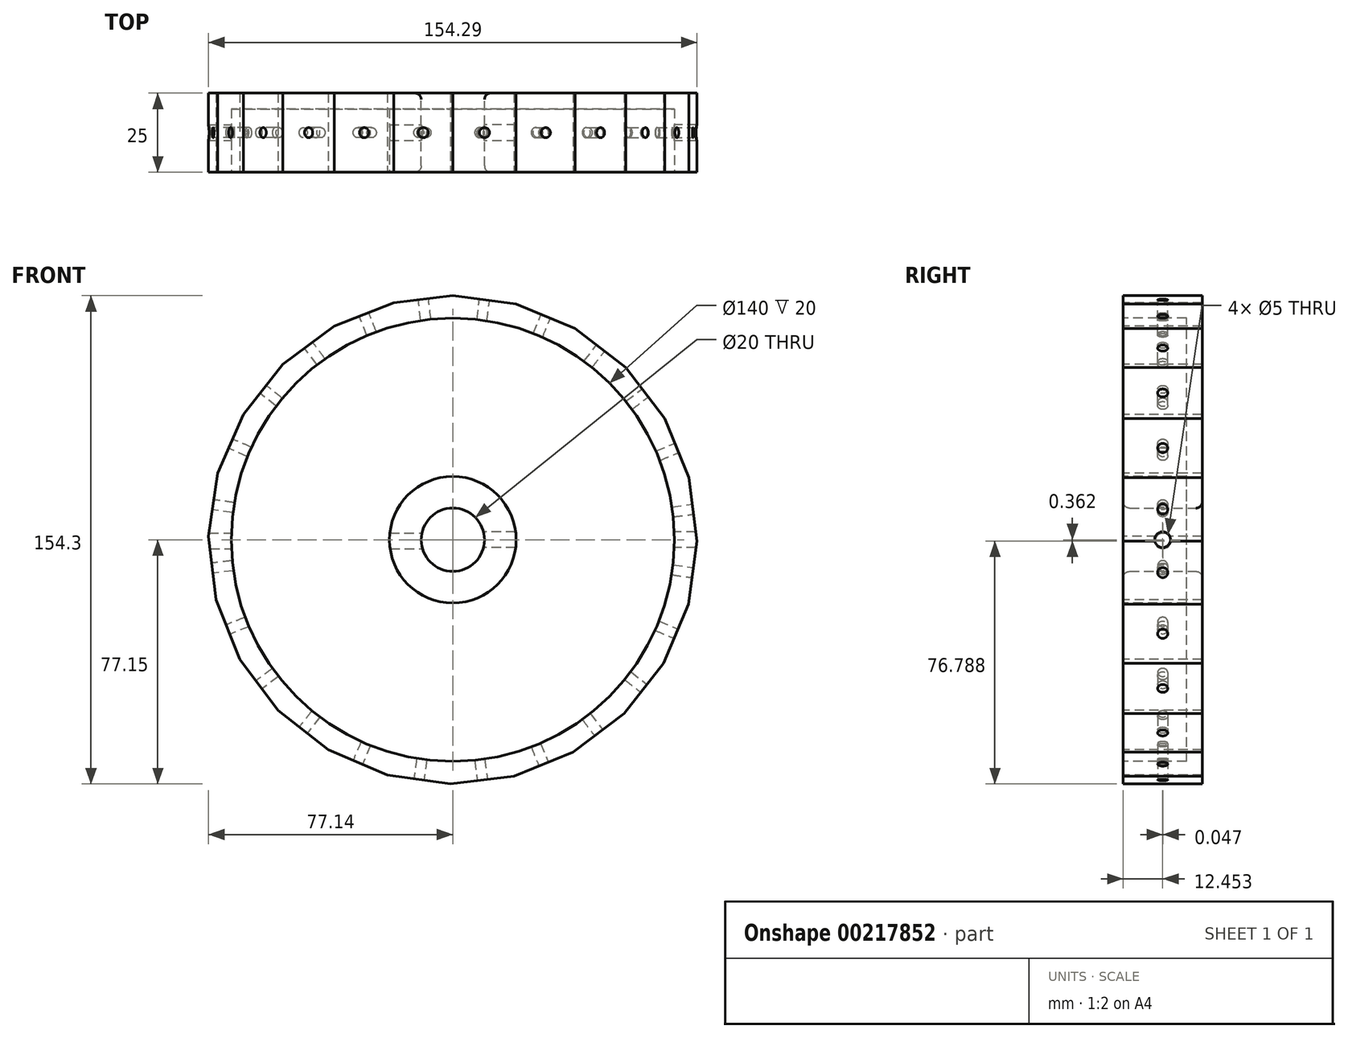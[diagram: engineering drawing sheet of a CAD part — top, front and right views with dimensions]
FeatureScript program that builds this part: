
annotation { "Feature Type Name" : "Feature", "Feature Type Description" : "" }
export const myFeature = defineFeature(function(context is Context, id is Id, definition is map)
    precondition{}
    {
        {
            var Q0;
            Q0=qCreatedBy(makeId("Front.planeOp"),FACE);
            var sketch = newSketch(context, id + "F0", { "sketchPlane" : qUnion([Q0])});
            skCircle(sketch, "E0", {"center": v(0, 0) * mm, "radius": 77.15 * mm});
            skCircle(sketch, "E1", {"center": v(0, 0) * mm, "radius": 10 * mm});
            skSolve(sketch);
        }
        {
            var Q0;
            Q0 = qSketchRegion(id + "F0", true);
            extrude(context, id + "F1", {"entities" : qUnion([Q0]), "depth" : 25 * mm});
        }
        {
            var Q0;
            Q0=makeQuery(id+"F1.opExtrude","CAP_FACE",FACE,{"disambiguationData":[OSD([sQuery(id+"F0.wireOp",EDGE,"E0"),sQuery(id+"F0.wireOp",EDGE,"E1")])],"isStart":false});
            var sketch = newSketch(context, id + "F2", { "sketchPlane" : qUnion([Q0])});
            skLineSegment(sketch, "E2", {"start": v(0, 0) * mm, "end": v(0, 77.15) * mm});
            skLineSegment(sketch, "E3", {"start": v(0, 0) * mm, "end": v(20.03, 74.5) * mm});
            skLineSegment(sketch, "E4", {"start": v(0, 77.15) * mm, "end": v(20.03, 74.5) * mm});
            skLineSegment(sketch, "E5", {"start": v(0, 0) * mm, "end": v(38.68, 66.75) * mm});
            skLineSegment(sketch, "E6", {"start": v(20.03, 74.5) * mm, "end": v(38.68, 66.75) * mm});
            skLineSegment(sketch, "E7", {"start": v(0, 0) * mm, "end": v(54.68, 54.43) * mm});
            skLineSegment(sketch, "E8", {"start": v(38.68, 66.75) * mm, "end": v(54.68, 54.43) * mm});
            skLineSegment(sketch, "E9", {"start": v(0, 0) * mm, "end": v(66.93, 38.37) * mm});
            skLineSegment(sketch, "E10", {"start": v(54.68, 54.43) * mm, "end": v(66.93, 38.37) * mm});
            skLineSegment(sketch, "E11", {"start": v(0, 0) * mm, "end": v(74.6, 19.68) * mm});
            skLineSegment(sketch, "E12", {"start": v(74.6, 19.68) * mm, "end": v(66.93, 38.37) * mm});
            skLineSegment(sketch, "E13", {"start": v(0, 0) * mm, "end": v(77.15, -0.36) * mm});
            skLineSegment(sketch, "E14", {"start": v(77.15, -0.36) * mm, "end": v(74.6, 19.68) * mm});
            skLineSegment(sketch, "E15", {"start": v(0, 0) * mm, "end": v(74.41, -20.38) * mm});
            skLineSegment(sketch, "E16", {"start": v(74.41, -20.38) * mm, "end": v(77.15, -0.36) * mm});
            skLineSegment(sketch, "E17", {"start": v(0, 0) * mm, "end": v(66.57, -39) * mm});
            skLineSegment(sketch, "E18", {"start": v(66.57, -39) * mm, "end": v(74.41, -20.38) * mm});
            skLineSegment(sketch, "E19", {"start": v(0, 0) * mm, "end": v(54.17, -54.94) * mm});
            skLineSegment(sketch, "E20", {"start": v(54.17, -54.94) * mm, "end": v(66.57, -39) * mm});
            skLineSegment(sketch, "E21", {"start": v(0, 0) * mm, "end": v(38.05, -67.11) * mm});
            skLineSegment(sketch, "E22", {"start": v(38.05, -67.11) * mm, "end": v(54.17, -54.94) * mm});
            skLineSegment(sketch, "E23", {"start": v(0, 0) * mm, "end": v(19.33, -74.7) * mm});
            skLineSegment(sketch, "E24", {"start": v(19.33, -74.7) * mm, "end": v(38.05, -67.11) * mm});
            skLineSegment(sketch, "E25", {"start": v(0, 0) * mm, "end": v(-0.72, -77.15) * mm});
            skLineSegment(sketch, "E26", {"start": v(-0.72, -77.15) * mm, "end": v(19.33, -74.7) * mm});
            skLineSegment(sketch, "E27", {"start": v(0, 0) * mm, "end": v(-20.72, -74.31) * mm});
            skLineSegment(sketch, "E28", {"start": v(-20.72, -74.31) * mm, "end": v(-0.72, -77.15) * mm});
            skLineSegment(sketch, "E29", {"start": v(0, 0) * mm, "end": v(-39.3, -66.39) * mm});
            skLineSegment(sketch, "E30", {"start": v(-39.3, -66.39) * mm, "end": v(-20.72, -74.31) * mm});
            skLineSegment(sketch, "E31", {"start": v(0, 0) * mm, "end": v(-55.19, -53.9) * mm});
            skLineSegment(sketch, "E32", {"start": v(-55.19, -53.9) * mm, "end": v(-39.3, -66.39) * mm});
            skLineSegment(sketch, "E33", {"start": v(0, 0) * mm, "end": v(-67.3, -37.74) * mm});
            skLineSegment(sketch, "E34", {"start": v(-67.3, -37.74) * mm, "end": v(-55.19, -53.9) * mm});
            skLineSegment(sketch, "E35", {"start": v(0, 0) * mm, "end": v(-74.78, -18.98) * mm});
            skLineSegment(sketch, "E36", {"start": v(-74.78, -18.98) * mm, "end": v(-67.3, -37.74) * mm});
            skLineSegment(sketch, "E37", {"start": v(0, 0) * mm, "end": v(-77.14, 1.09) * mm});
            skLineSegment(sketch, "E38", {"start": v(-77.14, 1.09) * mm, "end": v(-74.78, -18.98) * mm});
            skLineSegment(sketch, "E39", {"start": v(0, 0) * mm, "end": v(-74.22, 21.07) * mm});
            skLineSegment(sketch, "E40", {"start": v(-74.22, 21.07) * mm, "end": v(-77.14, 1.09) * mm});
            skLineSegment(sketch, "E41", {"start": v(0, 0) * mm, "end": v(-66.2, 39.62) * mm});
            skLineSegment(sketch, "E42", {"start": v(-66.2, 39.62) * mm, "end": v(-74.22, 21.07) * mm});
            skLineSegment(sketch, "E43", {"start": v(0, 0) * mm, "end": v(-53.65, 55.44) * mm});
            skLineSegment(sketch, "E44", {"start": v(-53.65, 55.44) * mm, "end": v(-66.2, 39.62) * mm});
            skLineSegment(sketch, "E45", {"start": v(0, 0) * mm, "end": v(-37.42, 67.47) * mm});
            skLineSegment(sketch, "E46", {"start": v(-37.42, 67.47) * mm, "end": v(-53.65, 55.44) * mm});
            skLineSegment(sketch, "E47", {"start": v(0, 0) * mm, "end": v(-18.62, 74.87) * mm});
            skLineSegment(sketch, "E48", {"start": v(-18.62, 74.87) * mm, "end": v(-37.42, 67.47) * mm});
            skLineSegment(sketch, "E49", {"start": v(-18.62, 74.87) * mm, "end": v(0, 77.15) * mm});
            skSolve(sketch);
        }
        {
            var Q0;
            {var subQ0=sQuery(id+"F2.wireOp",EDGE,"E4");Q0=makeQuery(id+"F2.imprint","IMPRINT",FACE,{"disambiguationData":[TD([[makeQuery(id+"F2.imprint","IMPRINT",EDGE,{"derivedFrom":subQ0}),1.0]])]});}
            var Q1;
            {var subQ0=sQuery(id+"F2.wireOp",EDGE,"E6");Q1=makeQuery(id+"F2.imprint","IMPRINT",FACE,{"disambiguationData":[TD([[makeQuery(id+"F2.imprint","IMPRINT",EDGE,{"derivedFrom":subQ0}),1.0]])]});}
            var Q2;
            {var subQ0=sQuery(id+"F2.wireOp",EDGE,"E8");Q2=makeQuery(id+"F2.imprint","IMPRINT",FACE,{"disambiguationData":[TD([[makeQuery(id+"F2.imprint","IMPRINT",EDGE,{"derivedFrom":subQ0}),1.0]])]});}
            var Q3;
            {var subQ0=sQuery(id+"F2.wireOp",EDGE,"E10");Q3=makeQuery(id+"F2.imprint","IMPRINT",FACE,{"disambiguationData":[TD([[makeQuery(id+"F2.imprint","IMPRINT",EDGE,{"derivedFrom":subQ0}),1.0]])]});}
            var Q4;
            {var subQ0=sQuery(id+"F2.wireOp",EDGE,"E12");Q4=makeQuery(id+"F2.imprint","IMPRINT",FACE,{"disambiguationData":[TD([[makeQuery(id+"F2.imprint","IMPRINT",EDGE,{"derivedFrom":subQ0}),-1.0]])]});}
            var Q5;
            {var subQ0=sQuery(id+"F2.wireOp",EDGE,"E14");Q5=makeQuery(id+"F2.imprint","IMPRINT",FACE,{"disambiguationData":[TD([[makeQuery(id+"F2.imprint","IMPRINT",EDGE,{"derivedFrom":subQ0}),-1.0]])]});}
            var Q6;
            {var subQ0=sQuery(id+"F2.wireOp",EDGE,"E16");Q6=makeQuery(id+"F2.imprint","IMPRINT",FACE,{"disambiguationData":[TD([[makeQuery(id+"F2.imprint","IMPRINT",EDGE,{"derivedFrom":subQ0}),-1.0]])]});}
            var Q7;
            {var subQ0=sQuery(id+"F2.wireOp",EDGE,"E18");Q7=makeQuery(id+"F2.imprint","IMPRINT",FACE,{"disambiguationData":[TD([[makeQuery(id+"F2.imprint","IMPRINT",EDGE,{"derivedFrom":subQ0}),-1.0]])]});}
            var Q8;
            {var subQ0=sQuery(id+"F2.wireOp",EDGE,"E20");Q8=makeQuery(id+"F2.imprint","IMPRINT",FACE,{"disambiguationData":[TD([[makeQuery(id+"F2.imprint","IMPRINT",EDGE,{"derivedFrom":subQ0}),-1.0]])]});}
            var Q9;
            {var subQ0=sQuery(id+"F2.wireOp",EDGE,"E22");Q9=makeQuery(id+"F2.imprint","IMPRINT",FACE,{"disambiguationData":[TD([[makeQuery(id+"F2.imprint","IMPRINT",EDGE,{"derivedFrom":subQ0}),-1.0]])]});}
            var Q10;
            {var subQ0=sQuery(id+"F2.wireOp",EDGE,"E24");Q10=makeQuery(id+"F2.imprint","IMPRINT",FACE,{"disambiguationData":[TD([[makeQuery(id+"F2.imprint","IMPRINT",EDGE,{"derivedFrom":subQ0}),-1.0]])]});}
            var Q11;
            {var subQ0=sQuery(id+"F2.wireOp",EDGE,"E26");Q11=makeQuery(id+"F2.imprint","IMPRINT",FACE,{"disambiguationData":[TD([[makeQuery(id+"F2.imprint","IMPRINT",EDGE,{"derivedFrom":subQ0}),-1.0]])]});}
            var Q12;
            {var subQ0=sQuery(id+"F2.wireOp",EDGE,"E28");Q12=makeQuery(id+"F2.imprint","IMPRINT",FACE,{"disambiguationData":[TD([[makeQuery(id+"F2.imprint","IMPRINT",EDGE,{"derivedFrom":subQ0}),-1.0]])]});}
            var Q13;
            {var subQ0=sQuery(id+"F2.wireOp",EDGE,"E30");Q13=makeQuery(id+"F2.imprint","IMPRINT",FACE,{"disambiguationData":[TD([[makeQuery(id+"F2.imprint","IMPRINT",EDGE,{"derivedFrom":subQ0}),-1.0]])]});}
            var Q14;
            {var subQ0=sQuery(id+"F2.wireOp",EDGE,"E32");Q14=makeQuery(id+"F2.imprint","IMPRINT",FACE,{"disambiguationData":[TD([[makeQuery(id+"F2.imprint","IMPRINT",EDGE,{"derivedFrom":subQ0}),-1.0]])]});}
            var Q15;
            {var subQ0=sQuery(id+"F2.wireOp",EDGE,"E34");Q15=makeQuery(id+"F2.imprint","IMPRINT",FACE,{"disambiguationData":[TD([[makeQuery(id+"F2.imprint","IMPRINT",EDGE,{"derivedFrom":subQ0}),-1.0]])]});}
            var Q16;
            {var subQ0=sQuery(id+"F2.wireOp",EDGE,"E36");Q16=makeQuery(id+"F2.imprint","IMPRINT",FACE,{"disambiguationData":[TD([[makeQuery(id+"F2.imprint","IMPRINT",EDGE,{"derivedFrom":subQ0}),-1.0]])]});}
            var Q17;
            {var subQ0=sQuery(id+"F2.wireOp",EDGE,"E38");Q17=makeQuery(id+"F2.imprint","IMPRINT",FACE,{"disambiguationData":[TD([[makeQuery(id+"F2.imprint","IMPRINT",EDGE,{"derivedFrom":subQ0}),-1.0]])]});}
            var Q18;
            {var subQ0=sQuery(id+"F2.wireOp",EDGE,"E40");Q18=makeQuery(id+"F2.imprint","IMPRINT",FACE,{"disambiguationData":[TD([[makeQuery(id+"F2.imprint","IMPRINT",EDGE,{"derivedFrom":subQ0}),-1.0]])]});}
            var Q19;
            {var subQ0=sQuery(id+"F2.wireOp",EDGE,"E42");Q19=makeQuery(id+"F2.imprint","IMPRINT",FACE,{"disambiguationData":[TD([[makeQuery(id+"F2.imprint","IMPRINT",EDGE,{"derivedFrom":subQ0}),-1.0]])]});}
            var Q20;
            {var subQ0=sQuery(id+"F2.wireOp",EDGE,"E44");Q20=makeQuery(id+"F2.imprint","IMPRINT",FACE,{"disambiguationData":[TD([[makeQuery(id+"F2.imprint","IMPRINT",EDGE,{"derivedFrom":subQ0}),-1.0]])]});}
            var Q21;
            {var subQ0=sQuery(id+"F2.wireOp",EDGE,"E46");Q21=makeQuery(id+"F2.imprint","IMPRINT",FACE,{"disambiguationData":[TD([[makeQuery(id+"F2.imprint","IMPRINT",EDGE,{"derivedFrom":subQ0}),-1.0]])]});}
            var Q22;
            {var subQ0=sQuery(id+"F2.wireOp",EDGE,"E48");Q22=makeQuery(id+"F2.imprint","IMPRINT",FACE,{"disambiguationData":[TD([[makeQuery(id+"F2.imprint","IMPRINT",EDGE,{"derivedFrom":subQ0}),-1.0]])]});}
            var Q23;
            {var subQ0=sQuery(id+"F2.wireOp",EDGE,"E49");Q23=makeQuery(id+"F2.imprint","IMPRINT",FACE,{"disambiguationData":[TD([[makeQuery(id+"F2.imprint","IMPRINT",EDGE,{"derivedFrom":subQ0}),1.0]])]});}
            extrude(context, id + "F3", {"entities" : qUnion([Q0, Q1, Q2, Q3, Q4, Q5, Q6, Q7, Q8, Q9, Q10, Q11, Q12, Q13, Q14, Q15, Q16, Q17, Q18, Q19, Q20, Q21, Q22, Q23]), "operationType" : NewBodyOperationType.REMOVE, "oppositeDirection" : true, "depth" : 25 * mm});
        }
        {
            var Q0;
            Q0=makeQuery(id+"F1.opExtrude","CAP_FACE",FACE,{"disambiguationData":[OSD([sQuery(id+"F0.wireOp",EDGE,"E0"),sQuery(id+"F0.wireOp",EDGE,"E1")])],"isStart":false});
            var sketch = newSketch(context, id + "F4", { "sketchPlane" : qUnion([Q0])});
            skCircle(sketch, "E50", {"center": v(0, 0) * mm, "radius": 10 * mm});
            skCircle(sketch, "E51", {"center": v(0, 0) * mm, "radius": 20 * mm});
            skCircle(sketch, "E52", {"center": v(0, 0) * mm, "radius": 70 * mm});
            skSolve(sketch);
        }
        {
            var Q0;
            Q0=makeQuery(id+"F4.imprint","IMPRINT",FACE,{"disambiguationData":[TD([[makeQuery(id+"F4.imprint","IMPRINT",EDGE,{"derivedFrom":sQuery(id+"F4.wireOp",EDGE,"E51")}),-1.0]])]});
            extrude(context, id + "F5", {"entities" : qUnion([Q0]), "operationType" : NewBodyOperationType.REMOVE, "oppositeDirection" : true, "depth" : 20 * mm});
        }
        {
            var Q0;
            Q0=makeQuery(id+"F1.opExtrude","CAP_EDGE",EDGE,{"disambiguationData":[OSD([sQuery(id+"F0.wireOp",EDGE,"E1")])],"isStart":true});
            var Q1;
            Q1=makeQuery(id+"F1.opExtrude","CAP_EDGE",EDGE,{"disambiguationData":[OSD([sQuery(id+"F0.wireOp",EDGE,"E1")])],"isStart":false});
            fillet(context, id + "F6", {"entities" : qUnion([Q0, Q1]), "radius" : 2 * mm, "tangentPropagation" : true, "allowEdgeOverflow" : false});
        }
        {
            var Q0;
            Q0=makeQuery(id+"F3.boolean.opBoolean","COPY",FACE,{"derivedFrom":makeQuery(id+"F3.opExtrude","SWEPT_FACE",FACE,{"disambiguationData":[OSD([sQuery(id+"F2.wireOp",EDGE,"E14")])]})});
            var sketch = newSketch(context, id + "F7", { "sketchPlane" : qUnion([Q0])});
            skCircle(sketch, "E53", {"center": v(-12.5, 0) * mm, "radius": 1.75 * mm});
            skPoint(sketch, "E53.centerSnap0", {"position": v(-25, 0) * mm});
            skSolve(sketch);
        }
        {
            var Q0;
            Q0=sQuery(id+"F7.wireOp",VERTEX,"E53.center");
            var Q1;
            Q1=makeQuery(id+"F1.opExtrude","SWEPT_BODY",BODY,{"disambiguationData":[OSD([sQuery(id+"F0.wireOp",EDGE,"E0"),sQuery(id+"F0.wireOp",EDGE,"E1")])]});
            hole(context, id + "F8", {"style" : HoleStyle.SIMPLE, "endStyle" : HoleEndStyle.BLIND, "standardTappedOrClearance" : lookupTablePath({ "standard" : "ISO", "engagement" : "75%", "pitch" : "0.75 mm", "size" : "M4", "type" : "Tapped" }), "standardBlindInLast" : lookupTablePath({ "standard" : "ISO", "engagement" : "75%", "pitch" : "0.75 mm", "size" : "M4", "type" : "Tapped" }), "holeDiameter" : 3.2 * mm, "holeDepth" : 20 * mm, "startFromSketch" : true, "locations" : qUnion([Q0]), "scope" : qUnion([Q1])});
        }
        {
            var Q0;
            Q0=makeQuery(id+"F3.boolean.opBoolean","COPY",FACE,{"derivedFrom":makeQuery(id+"F3.opExtrude","SWEPT_FACE",FACE,{"disambiguationData":[OSD([sQuery(id+"F2.wireOp",EDGE,"E16")])]})});
            var sketch = newSketch(context, id + "F9", { "sketchPlane" : qUnion([Q0])});
            skCircle(sketch, "E54", {"center": v(-12.5, 0) * mm, "radius": 1.75 * mm});
            skSolve(sketch);
        }
        {
            var Q0;
            Q0=sQuery(id+"F9.wireOp",VERTEX,"E54.center");
            var Q1;
            Q1=makeQuery(id+"F1.opExtrude","SWEPT_BODY",BODY,{"disambiguationData":[OSD([sQuery(id+"F0.wireOp",EDGE,"E0"),sQuery(id+"F0.wireOp",EDGE,"E1")])]});
            hole(context, id + "F10", {"style" : HoleStyle.SIMPLE, "endStyle" : HoleEndStyle.BLIND, "standardTappedOrClearance" : lookupTablePath({ "standard" : "ISO", "engagement" : "75%", "pitch" : "0.75 mm", "size" : "M4", "type" : "Tapped" }), "standardBlindInLast" : lookupTablePath({ "standard" : "ISO", "engagement" : "75%", "pitch" : "0.75 mm", "size" : "M4", "type" : "Tapped" }), "holeDiameter" : 3.2 * mm, "holeDepth" : 20 * mm, "startFromSketch" : true, "locations" : qUnion([Q0]), "scope" : qUnion([Q1])});
        }
        {
            var Q0;
            Q0=makeQuery(id+"F3.boolean.opBoolean","COPY",FACE,{"derivedFrom":makeQuery(id+"F3.opExtrude","SWEPT_FACE",FACE,{"disambiguationData":[OSD([sQuery(id+"F2.wireOp",EDGE,"E18")])]})});
            var sketch = newSketch(context, id + "F11", { "sketchPlane" : qUnion([Q0])});
            skCircle(sketch, "E55", {"center": v(-12.5, 0) * mm, "radius": 1.75 * mm});
            skSolve(sketch);
        }
        {
            var Q0;
            Q0=sQuery(id+"F11.wireOp",VERTEX,"E55.center");
            var Q1;
            Q1=makeQuery(id+"F1.opExtrude","SWEPT_BODY",BODY,{"disambiguationData":[OSD([sQuery(id+"F0.wireOp",EDGE,"E0"),sQuery(id+"F0.wireOp",EDGE,"E1")])]});
            hole(context, id + "F12", {"style" : HoleStyle.SIMPLE, "endStyle" : HoleEndStyle.BLIND, "standardTappedOrClearance" : lookupTablePath({ "standard" : "ISO", "engagement" : "75%", "pitch" : "0.75 mm", "size" : "M4", "type" : "Tapped" }), "standardBlindInLast" : lookupTablePath({ "standard" : "ISO", "engagement" : "75%", "pitch" : "0.75 mm", "size" : "M4", "type" : "Tapped" }), "holeDiameter" : 3.2 * mm, "holeDepth" : 20 * mm, "startFromSketch" : true, "locations" : qUnion([Q0]), "scope" : qUnion([Q1])});
        }
        {
            var Q0;
            Q0=makeQuery(id+"F3.boolean.opBoolean","COPY",FACE,{"derivedFrom":makeQuery(id+"F3.opExtrude","SWEPT_FACE",FACE,{"disambiguationData":[OSD([sQuery(id+"F2.wireOp",EDGE,"E20")])]})});
            var sketch = newSketch(context, id + "F13", { "sketchPlane" : qUnion([Q0])});
            skCircle(sketch, "E56", {"center": v(-12.5, 0) * mm, "radius": 1.75 * mm});
            skSolve(sketch);
        }
        {
            var Q0;
            Q0=sQuery(id+"F13.wireOp",VERTEX,"E56.center");
            var Q1;
            Q1=makeQuery(id+"F1.opExtrude","SWEPT_BODY",BODY,{"disambiguationData":[OSD([sQuery(id+"F0.wireOp",EDGE,"E0"),sQuery(id+"F0.wireOp",EDGE,"E1")])]});
            hole(context, id + "F14", {"style" : HoleStyle.SIMPLE, "endStyle" : HoleEndStyle.BLIND, "standardTappedOrClearance" : lookupTablePath({ "standard" : "ISO", "engagement" : "75%", "pitch" : "0.75 mm", "size" : "M4", "type" : "Tapped" }), "standardBlindInLast" : lookupTablePath({ "standard" : "ISO", "engagement" : "75%", "pitch" : "0.75 mm", "size" : "M4", "type" : "Tapped" }), "holeDiameter" : 3.2 * mm, "holeDepth" : 20 * mm, "startFromSketch" : true, "locations" : qUnion([Q0]), "scope" : qUnion([Q1])});
        }
        {
            var Q0;
            Q0=makeQuery(id+"F3.boolean.opBoolean","COPY",FACE,{"derivedFrom":makeQuery(id+"F3.opExtrude","SWEPT_FACE",FACE,{"disambiguationData":[OSD([sQuery(id+"F2.wireOp",EDGE,"E22")])]})});
            var sketch = newSketch(context, id + "F15", { "sketchPlane" : qUnion([Q0])});
            skCircle(sketch, "E57", {"center": v(0, 12.5) * mm, "radius": 1.75 * mm});
            skPoint(sketch, "E57.centerSnap0", {"position": v(-10.1, 12.5) * mm});
            skSolve(sketch);
        }
        {
            var Q0;
            Q0=sQuery(id+"F15.wireOp",VERTEX,"E57.center");
            var Q1;
            Q1=makeQuery(id+"F1.opExtrude","SWEPT_BODY",BODY,{"disambiguationData":[OSD([sQuery(id+"F0.wireOp",EDGE,"E0"),sQuery(id+"F0.wireOp",EDGE,"E1")])]});
            hole(context, id + "F16", {"style" : HoleStyle.SIMPLE, "endStyle" : HoleEndStyle.BLIND, "standardTappedOrClearance" : lookupTablePath({ "standard" : "ISO", "engagement" : "75%", "pitch" : "0.75 mm", "size" : "M4", "type" : "Tapped" }), "standardBlindInLast" : lookupTablePath({ "standard" : "ISO", "engagement" : "75%", "pitch" : "0.75 mm", "size" : "M4", "type" : "Tapped" }), "holeDiameter" : 3.2 * mm, "holeDepth" : 20 * mm, "startFromSketch" : true, "locations" : qUnion([Q0]), "scope" : qUnion([Q1])});
        }
        {
            var Q0;
            Q0=makeQuery(id+"F3.boolean.opBoolean","COPY",FACE,{"derivedFrom":makeQuery(id+"F3.opExtrude","SWEPT_FACE",FACE,{"disambiguationData":[OSD([sQuery(id+"F2.wireOp",EDGE,"E24")])]})});
            var sketch = newSketch(context, id + "F17", { "sketchPlane" : qUnion([Q0])});
            skCircle(sketch, "E58", {"center": v(0, 12.5) * mm, "radius": 1.75 * mm});
            skSolve(sketch);
        }
        {
            var Q0;
            Q0=sQuery(id+"F17.wireOp",VERTEX,"E58.center");
            var Q1;
            Q1=makeQuery(id+"F1.opExtrude","SWEPT_BODY",BODY,{"disambiguationData":[OSD([sQuery(id+"F0.wireOp",EDGE,"E0"),sQuery(id+"F0.wireOp",EDGE,"E1")])]});
            hole(context, id + "F18", {"style" : HoleStyle.SIMPLE, "endStyle" : HoleEndStyle.BLIND, "standardTappedOrClearance" : lookupTablePath({ "standard" : "ISO", "engagement" : "75%", "pitch" : "0.75 mm", "size" : "M4", "type" : "Tapped" }), "standardBlindInLast" : lookupTablePath({ "standard" : "ISO", "engagement" : "75%", "pitch" : "0.75 mm", "size" : "M4", "type" : "Tapped" }), "holeDiameter" : 3.2 * mm, "holeDepth" : 20 * mm, "startFromSketch" : true, "locations" : qUnion([Q0]), "scope" : qUnion([Q1])});
        }
        {
            var Q0;
            Q0=makeQuery(id+"F3.boolean.opBoolean","COPY",FACE,{"derivedFrom":makeQuery(id+"F3.opExtrude","SWEPT_FACE",FACE,{"disambiguationData":[OSD([sQuery(id+"F2.wireOp",EDGE,"E26")])]})});
            var sketch = newSketch(context, id + "F19", { "sketchPlane" : qUnion([Q0])});
            skCircle(sketch, "E59", {"center": v(0, 12.5) * mm, "radius": 1.75 * mm});
            skSolve(sketch);
        }
        {
            var Q0;
            Q0=sQuery(id+"F19.wireOp",VERTEX,"E59.center");
            var Q1;
            Q1=makeQuery(id+"F1.opExtrude","SWEPT_BODY",BODY,{"disambiguationData":[OSD([sQuery(id+"F0.wireOp",EDGE,"E0"),sQuery(id+"F0.wireOp",EDGE,"E1")])]});
            hole(context, id + "F20", {"style" : HoleStyle.SIMPLE, "endStyle" : HoleEndStyle.BLIND, "standardTappedOrClearance" : lookupTablePath({ "standard" : "ISO", "engagement" : "75%", "pitch" : "0.75 mm", "size" : "M4", "type" : "Tapped" }), "standardBlindInLast" : lookupTablePath({ "standard" : "ISO", "engagement" : "75%", "pitch" : "0.75 mm", "size" : "M4", "type" : "Tapped" }), "holeDiameter" : 3.2 * mm, "holeDepth" : 20 * mm, "startFromSketch" : true, "locations" : qUnion([Q0]), "scope" : qUnion([Q1])});
        }
        {
            var Q0;
            Q0=makeQuery(id+"F3.boolean.opBoolean","COPY",FACE,{"derivedFrom":makeQuery(id+"F3.opExtrude","SWEPT_FACE",FACE,{"disambiguationData":[OSD([sQuery(id+"F2.wireOp",EDGE,"E28")])]})});
            var sketch = newSketch(context, id + "F21", { "sketchPlane" : qUnion([Q0])});
            skCircle(sketch, "E60", {"center": v(0, 12.5) * mm, "radius": 1.75 * mm});
            skPoint(sketch, "E60.centerSnap0", {"position": v(-10.1, 12.5) * mm});
            skSolve(sketch);
        }
        {
            var Q0;
            Q0=sQuery(id+"F21.wireOp",VERTEX,"E60.center");
            var Q1;
            Q1=makeQuery(id+"F1.opExtrude","SWEPT_BODY",BODY,{"disambiguationData":[OSD([sQuery(id+"F0.wireOp",EDGE,"E0"),sQuery(id+"F0.wireOp",EDGE,"E1")])]});
            hole(context, id + "F22", {"style" : HoleStyle.SIMPLE, "endStyle" : HoleEndStyle.BLIND, "standardTappedOrClearance" : lookupTablePath({ "standard" : "ISO", "engagement" : "75%", "pitch" : "0.75 mm", "size" : "M4", "type" : "Tapped" }), "standardBlindInLast" : lookupTablePath({ "standard" : "ISO", "engagement" : "75%", "pitch" : "0.75 mm", "size" : "M4", "type" : "Tapped" }), "holeDiameter" : 3.2 * mm, "holeDepth" : 20 * mm, "startFromSketch" : true, "locations" : qUnion([Q0]), "scope" : qUnion([Q1])});
        }
        {
            var Q0;
            Q0=makeQuery(id+"F3.boolean.opBoolean","COPY",FACE,{"derivedFrom":makeQuery(id+"F3.opExtrude","SWEPT_FACE",FACE,{"disambiguationData":[OSD([sQuery(id+"F2.wireOp",EDGE,"E30")])]})});
            var sketch = newSketch(context, id + "F23", { "sketchPlane" : qUnion([Q0])});
            skCircle(sketch, "E61", {"center": v(0, 12.5) * mm, "radius": 1.75 * mm});
            skPoint(sketch, "E61.centerSnap0", {"position": v(10.1, 12.5) * mm});
            skSolve(sketch);
        }
        {
            var Q0;
            Q0=sQuery(id+"F23.wireOp",VERTEX,"E61.center");
            var Q1;
            Q1=makeQuery(id+"F1.opExtrude","SWEPT_BODY",BODY,{"disambiguationData":[OSD([sQuery(id+"F0.wireOp",EDGE,"E0"),sQuery(id+"F0.wireOp",EDGE,"E1")])]});
            hole(context, id + "F24", {"style" : HoleStyle.SIMPLE, "endStyle" : HoleEndStyle.BLIND, "standardTappedOrClearance" : lookupTablePath({ "standard" : "ISO", "engagement" : "75%", "pitch" : "0.75 mm", "size" : "M4", "type" : "Tapped" }), "standardBlindInLast" : lookupTablePath({ "standard" : "ISO", "engagement" : "75%", "pitch" : "0.75 mm", "size" : "M4", "type" : "Tapped" }), "holeDiameter" : 3.2 * mm, "holeDepth" : 20 * mm, "startFromSketch" : true, "locations" : qUnion([Q0]), "scope" : qUnion([Q1])});
        }
        {
            var Q0;
            Q0=makeQuery(id+"F3.boolean.opBoolean","COPY",FACE,{"derivedFrom":makeQuery(id+"F3.opExtrude","SWEPT_FACE",FACE,{"disambiguationData":[OSD([sQuery(id+"F2.wireOp",EDGE,"E32")])]})});
            var sketch = newSketch(context, id + "F25", { "sketchPlane" : qUnion([Q0])});
            skCircle(sketch, "E62", {"center": v(0, 12.5) * mm, "radius": 1.75 * mm});
            skPoint(sketch, "E62.centerSnap0", {"position": v(10.1, 12.5) * mm});
            skSolve(sketch);
        }
        {
            var Q0;
            Q0=sQuery(id+"F25.wireOp",VERTEX,"E62.center");
            var Q1;
            Q1=makeQuery(id+"F1.opExtrude","SWEPT_BODY",BODY,{"disambiguationData":[OSD([sQuery(id+"F0.wireOp",EDGE,"E0"),sQuery(id+"F0.wireOp",EDGE,"E1")])]});
            hole(context, id + "F26", {"style" : HoleStyle.SIMPLE, "endStyle" : HoleEndStyle.BLIND, "standardTappedOrClearance" : lookupTablePath({ "standard" : "ISO", "engagement" : "75%", "pitch" : "0.75 mm", "size" : "M4", "type" : "Tapped" }), "standardBlindInLast" : lookupTablePath({ "standard" : "ISO", "engagement" : "75%", "pitch" : "0.75 mm", "size" : "M4", "type" : "Tapped" }), "holeDiameter" : 3.2 * mm, "holeDepth" : 20 * mm, "startFromSketch" : true, "locations" : qUnion([Q0]), "scope" : qUnion([Q1])});
        }
        {
            var Q0;
            Q0=makeQuery(id+"F3.boolean.opBoolean","COPY",FACE,{"derivedFrom":makeQuery(id+"F3.opExtrude","SWEPT_FACE",FACE,{"disambiguationData":[OSD([sQuery(id+"F2.wireOp",EDGE,"E34")])]})});
            var sketch = newSketch(context, id + "F27", { "sketchPlane" : qUnion([Q0])});
            skCircle(sketch, "E63", {"center": v(12.5, 0) * mm, "radius": 1.75 * mm});
            skPoint(sketch, "E63.centerSnap0", {"position": v(12.5, -10.1) * mm});
            skPoint(sketch, "E63.centerSnap1", {"position": v(0, 0) * mm});
            skSolve(sketch);
        }
        {
            var Q0;
            Q0=sQuery(id+"F27.wireOp",VERTEX,"E63.center");
            var Q1;
            Q1=makeQuery(id+"F1.opExtrude","SWEPT_BODY",BODY,{"disambiguationData":[OSD([sQuery(id+"F0.wireOp",EDGE,"E0"),sQuery(id+"F0.wireOp",EDGE,"E1")])]});
            hole(context, id + "F28", {"style" : HoleStyle.SIMPLE, "endStyle" : HoleEndStyle.BLIND, "standardTappedOrClearance" : lookupTablePath({ "standard" : "ISO", "engagement" : "75%", "pitch" : "0.75 mm", "size" : "M4", "type" : "Tapped" }), "standardBlindInLast" : lookupTablePath({ "standard" : "ISO", "engagement" : "75%", "pitch" : "0.75 mm", "size" : "M4", "type" : "Tapped" }), "holeDiameter" : 3.2 * mm, "holeDepth" : 20 * mm, "startFromSketch" : true, "locations" : qUnion([Q0]), "scope" : qUnion([Q1])});
        }
        {
            var Q0;
            Q0=makeQuery(id+"F3.boolean.opBoolean","COPY",FACE,{"derivedFrom":makeQuery(id+"F3.opExtrude","SWEPT_FACE",FACE,{"disambiguationData":[OSD([sQuery(id+"F2.wireOp",EDGE,"E36")])]})});
            var sketch = newSketch(context, id + "F29", { "sketchPlane" : qUnion([Q0])});
            skCircle(sketch, "E64", {"center": v(12.5, 0) * mm, "radius": 1.75 * mm});
            skPoint(sketch, "E64.centerSnap0", {"position": v(12.5, -10.1) * mm});
            skSolve(sketch);
        }
        {
            var Q0;
            Q0=sQuery(id+"F29.wireOp",VERTEX,"E64.center");
            var Q1;
            Q1=makeQuery(id+"F1.opExtrude","SWEPT_BODY",BODY,{"disambiguationData":[OSD([sQuery(id+"F0.wireOp",EDGE,"E0"),sQuery(id+"F0.wireOp",EDGE,"E1")])]});
            hole(context, id + "F30", {"style" : HoleStyle.SIMPLE, "endStyle" : HoleEndStyle.BLIND, "standardTappedOrClearance" : lookupTablePath({ "standard" : "ISO", "engagement" : "75%", "pitch" : "0.75 mm", "size" : "M4", "type" : "Tapped" }), "standardBlindInLast" : lookupTablePath({ "standard" : "ISO", "engagement" : "75%", "pitch" : "0.75 mm", "size" : "M4", "type" : "Tapped" }), "holeDiameter" : 3.2 * mm, "holeDepth" : 20 * mm, "startFromSketch" : true, "locations" : qUnion([Q0]), "scope" : qUnion([Q1])});
        }
        {
            var Q0;
            Q0=makeQuery(id+"F3.boolean.opBoolean","COPY",FACE,{"derivedFrom":makeQuery(id+"F3.opExtrude","SWEPT_FACE",FACE,{"disambiguationData":[OSD([sQuery(id+"F2.wireOp",EDGE,"E38")])]})});
            var sketch = newSketch(context, id + "F31", { "sketchPlane" : qUnion([Q0])});
            skCircle(sketch, "E65", {"center": v(12.5, 0) * mm, "radius": 1.75 * mm});
            skPoint(sketch, "E65.centerSnap0", {"position": v(12.5, -10.1) * mm});
            skSolve(sketch);
        }
        {
            var Q0;
            Q0=sQuery(id+"F31.wireOp",VERTEX,"E65.center");
            var Q1;
            Q1=makeQuery(id+"F1.opExtrude","SWEPT_BODY",BODY,{"disambiguationData":[OSD([sQuery(id+"F0.wireOp",EDGE,"E0"),sQuery(id+"F0.wireOp",EDGE,"E1")])]});
            hole(context, id + "F32", {"style" : HoleStyle.SIMPLE, "endStyle" : HoleEndStyle.BLIND, "standardTappedOrClearance" : lookupTablePath({ "standard" : "ISO", "engagement" : "75%", "pitch" : "0.75 mm", "size" : "M4", "type" : "Tapped" }), "standardBlindInLast" : lookupTablePath({ "standard" : "ISO", "engagement" : "75%", "pitch" : "0.75 mm", "size" : "M4", "type" : "Tapped" }), "holeDiameter" : 3.2 * mm, "holeDepth" : 20 * mm, "startFromSketch" : true, "locations" : qUnion([Q0]), "scope" : qUnion([Q1])});
        }
        {
            var Q0;
            Q0=makeQuery(id+"F3.boolean.opBoolean","COPY",FACE,{"derivedFrom":makeQuery(id+"F3.opExtrude","SWEPT_FACE",FACE,{"disambiguationData":[OSD([sQuery(id+"F2.wireOp",EDGE,"E40")])]})});
            var sketch = newSketch(context, id + "F33", { "sketchPlane" : qUnion([Q0])});
            skCircle(sketch, "E66", {"center": v(12.5, 0) * mm, "radius": 1.75 * mm});
            skPoint(sketch, "E66.centerSnap0", {"position": v(12.5, -10.1) * mm});
            skSolve(sketch);
        }
        {
            var Q0;
            Q0=sQuery(id+"F33.wireOp",VERTEX,"E66.center");
            var Q1;
            Q1=makeQuery(id+"F1.opExtrude","SWEPT_BODY",BODY,{"disambiguationData":[OSD([sQuery(id+"F0.wireOp",EDGE,"E0"),sQuery(id+"F0.wireOp",EDGE,"E1")])]});
            hole(context, id + "F34", {"style" : HoleStyle.SIMPLE, "endStyle" : HoleEndStyle.BLIND, "standardTappedOrClearance" : lookupTablePath({ "standard" : "ISO", "engagement" : "75%", "pitch" : "0.75 mm", "size" : "M4", "type" : "Tapped" }), "standardBlindInLast" : lookupTablePath({ "standard" : "ISO", "engagement" : "75%", "pitch" : "0.75 mm", "size" : "M4", "type" : "Tapped" }), "holeDiameter" : 3.2 * mm, "holeDepth" : 20 * mm, "startFromSketch" : true, "locations" : qUnion([Q0]), "scope" : qUnion([Q1])});
        }
        {
            var Q0;
            Q0=makeQuery(id+"F3.boolean.opBoolean","COPY",FACE,{"derivedFrom":makeQuery(id+"F3.opExtrude","SWEPT_FACE",FACE,{"disambiguationData":[OSD([sQuery(id+"F2.wireOp",EDGE,"E42")])]})});
            var sketch = newSketch(context, id + "F35", { "sketchPlane" : qUnion([Q0])});
            skCircle(sketch, "E67", {"center": v(12.5, 0) * mm, "radius": 1.75 * mm});
            skPoint(sketch, "E67.centerSnap0", {"position": v(12.5, -10.1) * mm});
            skSolve(sketch);
        }
        {
            var Q0;
            Q0=sQuery(id+"F35.wireOp",VERTEX,"E67.center");
            var Q1;
            Q1=makeQuery(id+"F1.opExtrude","SWEPT_BODY",BODY,{"disambiguationData":[OSD([sQuery(id+"F0.wireOp",EDGE,"E0"),sQuery(id+"F0.wireOp",EDGE,"E1")])]});
            hole(context, id + "F36", {"style" : HoleStyle.SIMPLE, "endStyle" : HoleEndStyle.BLIND, "standardTappedOrClearance" : lookupTablePath({ "standard" : "ISO", "engagement" : "75%", "pitch" : "0.75 mm", "size" : "M4", "type" : "Tapped" }), "standardBlindInLast" : lookupTablePath({ "standard" : "ISO", "engagement" : "75%", "pitch" : "0.75 mm", "size" : "M4", "type" : "Tapped" }), "holeDiameter" : 3.2 * mm, "holeDepth" : 20 * mm, "startFromSketch" : true, "locations" : qUnion([Q0]), "scope" : qUnion([Q1])});
        }
        {
            var Q0;
            Q0=makeQuery(id+"F3.boolean.opBoolean","COPY",FACE,{"derivedFrom":makeQuery(id+"F3.opExtrude","SWEPT_FACE",FACE,{"disambiguationData":[OSD([sQuery(id+"F2.wireOp",EDGE,"E44")])]})});
            var sketch = newSketch(context, id + "F37", { "sketchPlane" : qUnion([Q0])});
            skCircle(sketch, "E68", {"center": v(12.5, 0) * mm, "radius": 1.75 * mm});
            skPoint(sketch, "E68.centerSnap0", {"position": v(12.5, -10.1) * mm});
            skSolve(sketch);
        }
        {
            var Q0;
            Q0=sQuery(id+"F37.wireOp",VERTEX,"E68.center");
            var Q1;
            Q1=makeQuery(id+"F1.opExtrude","SWEPT_BODY",BODY,{"disambiguationData":[OSD([sQuery(id+"F0.wireOp",EDGE,"E0"),sQuery(id+"F0.wireOp",EDGE,"E1")])]});
            hole(context, id + "F38", {"style" : HoleStyle.SIMPLE, "endStyle" : HoleEndStyle.BLIND, "standardTappedOrClearance" : lookupTablePath({ "standard" : "ISO", "engagement" : "75%", "pitch" : "0.75 mm", "size" : "M4", "type" : "Tapped" }), "standardBlindInLast" : lookupTablePath({ "standard" : "ISO", "engagement" : "75%", "pitch" : "0.75 mm", "size" : "M4", "type" : "Tapped" }), "holeDiameter" : 3.2 * mm, "holeDepth" : 20 * mm, "startFromSketch" : true, "locations" : qUnion([Q0]), "scope" : qUnion([Q1])});
        }
        {
            var Q0;
            Q0=makeQuery(id+"F3.boolean.opBoolean","COPY",FACE,{"derivedFrom":makeQuery(id+"F3.opExtrude","SWEPT_FACE",FACE,{"disambiguationData":[OSD([sQuery(id+"F2.wireOp",EDGE,"E46")])]})});
            var sketch = newSketch(context, id + "F39", { "sketchPlane" : qUnion([Q0])});
            skCircle(sketch, "E69", {"center": v(0, -12.5) * mm, "radius": 1.75 * mm});
            skPoint(sketch, "E69.centerSnap0", {"position": v(-10.1, -12.5) * mm});
            skPoint(sketch, "E69.centerSnap1", {"position": v(0, 0) * mm});
            skSolve(sketch);
        }
        {
            var Q0;
            Q0=sQuery(id+"F39.wireOp",VERTEX,"E69.center");
            var Q1;
            Q1=makeQuery(id+"F1.opExtrude","SWEPT_BODY",BODY,{"disambiguationData":[OSD([sQuery(id+"F0.wireOp",EDGE,"E0"),sQuery(id+"F0.wireOp",EDGE,"E1")])]});
            hole(context, id + "F40", {"style" : HoleStyle.SIMPLE, "endStyle" : HoleEndStyle.BLIND, "standardTappedOrClearance" : lookupTablePath({ "standard" : "ISO", "engagement" : "75%", "pitch" : "0.75 mm", "size" : "M4", "type" : "Tapped" }), "standardBlindInLast" : lookupTablePath({ "standard" : "ISO", "engagement" : "75%", "pitch" : "0.75 mm", "size" : "M4", "type" : "Tapped" }), "holeDiameter" : 3.2 * mm, "holeDepth" : 20 * mm, "startFromSketch" : true, "locations" : qUnion([Q0]), "scope" : qUnion([Q1])});
        }
        {
            var Q0;
            Q0=makeQuery(id+"F3.boolean.opBoolean","COPY",FACE,{"derivedFrom":makeQuery(id+"F3.opExtrude","SWEPT_FACE",FACE,{"disambiguationData":[OSD([sQuery(id+"F2.wireOp",EDGE,"E48")])]})});
            var sketch = newSketch(context, id + "F41", { "sketchPlane" : qUnion([Q0])});
            skCircle(sketch, "E70", {"center": v(0, -12.5) * mm, "radius": 1.75 * mm});
            skPoint(sketch, "E70.centerSnap0", {"position": v(-10.1, -12.5) * mm});
            skPoint(sketch, "E70.centerSnap1", {"position": v(0, 0) * mm});
            skSolve(sketch);
        }
        {
            var Q0;
            Q0=sQuery(id+"F41.wireOp",VERTEX,"E70.center");
            var Q1;
            Q1=makeQuery(id+"F1.opExtrude","SWEPT_BODY",BODY,{"disambiguationData":[OSD([sQuery(id+"F0.wireOp",EDGE,"E0"),sQuery(id+"F0.wireOp",EDGE,"E1")])]});
            hole(context, id + "F42", {"style" : HoleStyle.SIMPLE, "endStyle" : HoleEndStyle.BLIND, "standardTappedOrClearance" : lookupTablePath({ "standard" : "ISO", "engagement" : "75%", "pitch" : "0.75 mm", "size" : "M4", "type" : "Tapped" }), "standardBlindInLast" : lookupTablePath({ "standard" : "ISO", "engagement" : "75%", "pitch" : "0.75 mm", "size" : "M4", "type" : "Tapped" }), "holeDiameter" : 3.2 * mm, "holeDepth" : 20 * mm, "startFromSketch" : true, "locations" : qUnion([Q0]), "scope" : qUnion([Q1])});
        }
        {
            var Q0;
            Q0=makeQuery(id+"F3.boolean.opBoolean","COPY",FACE,{"derivedFrom":makeQuery(id+"F3.opExtrude","SWEPT_FACE",FACE,{"disambiguationData":[OSD([sQuery(id+"F2.wireOp",EDGE,"E49")])]})});
            var sketch = newSketch(context, id + "F43", { "sketchPlane" : qUnion([Q0])});
            skCircle(sketch, "E71", {"center": v(0, -12.5) * mm, "radius": 1.75 * mm});
            skPoint(sketch, "E71.centerSnap0", {"position": v(-9.38, -12.5) * mm});
            skSolve(sketch);
        }
        {
            var Q0;
            Q0=sQuery(id+"F43.wireOp",VERTEX,"E71.center");
            var Q1;
            Q1=makeQuery(id+"F1.opExtrude","SWEPT_BODY",BODY,{"disambiguationData":[OSD([sQuery(id+"F0.wireOp",EDGE,"E0"),sQuery(id+"F0.wireOp",EDGE,"E1")])]});
            hole(context, id + "F44", {"style" : HoleStyle.SIMPLE, "endStyle" : HoleEndStyle.BLIND, "standardTappedOrClearance" : lookupTablePath({ "standard" : "ISO", "engagement" : "75%", "pitch" : "0.75 mm", "size" : "M4", "type" : "Tapped" }), "standardBlindInLast" : lookupTablePath({ "standard" : "ISO", "engagement" : "75%", "pitch" : "0.75 mm", "size" : "M4", "type" : "Tapped" }), "holeDiameter" : 3.2 * mm, "holeDepth" : 20 * mm, "startFromSketch" : true, "locations" : qUnion([Q0]), "scope" : qUnion([Q1])});
        }
        {
            var Q0;
            Q0=makeQuery(id+"F3.boolean.opBoolean","COPY",FACE,{"derivedFrom":makeQuery(id+"F3.opExtrude","SWEPT_FACE",FACE,{"disambiguationData":[OSD([sQuery(id+"F2.wireOp",EDGE,"E4")])]})});
            var sketch = newSketch(context, id + "F45", { "sketchPlane" : qUnion([Q0])});
            skCircle(sketch, "E72", {"center": v(0, -12.5) * mm, "radius": 1.75 * mm});
            skPoint(sketch, "E72.centerSnap0", {"position": v(-10.1, -12.5) * mm});
            skSolve(sketch);
        }
        {
            var Q0;
            Q0=sQuery(id+"F45.wireOp",VERTEX,"E72.center");
            var Q1;
            Q1=makeQuery(id+"F1.opExtrude","SWEPT_BODY",BODY,{"disambiguationData":[OSD([sQuery(id+"F0.wireOp",EDGE,"E0"),sQuery(id+"F0.wireOp",EDGE,"E1")])]});
            hole(context, id + "F46", {"style" : HoleStyle.SIMPLE, "endStyle" : HoleEndStyle.BLIND, "standardTappedOrClearance" : lookupTablePath({ "standard" : "ISO", "engagement" : "75%", "pitch" : "0.75 mm", "size" : "M4", "type" : "Tapped" }), "standardBlindInLast" : lookupTablePath({ "standard" : "ISO", "engagement" : "75%", "pitch" : "0.75 mm", "size" : "M4", "type" : "Tapped" }), "holeDiameter" : 3.2 * mm, "holeDepth" : 20 * mm, "startFromSketch" : true, "locations" : qUnion([Q0]), "scope" : qUnion([Q1])});
        }
        {
            var Q0;
            Q0=makeQuery(id+"F3.boolean.opBoolean","COPY",FACE,{"derivedFrom":makeQuery(id+"F3.opExtrude","SWEPT_FACE",FACE,{"disambiguationData":[OSD([sQuery(id+"F2.wireOp",EDGE,"E6")])]})});
            var sketch = newSketch(context, id + "F47", { "sketchPlane" : qUnion([Q0])});
            skCircle(sketch, "E73", {"center": v(0, -12.5) * mm, "radius": 1.75 * mm});
            skPoint(sketch, "E73.centerSnap0", {"position": v(-10.1, -12.5) * mm});
            skSolve(sketch);
        }
        {
            var Q0;
            Q0=sQuery(id+"F47.wireOp",VERTEX,"E73.center");
            var Q1;
            Q1=makeQuery(id+"F1.opExtrude","SWEPT_BODY",BODY,{"disambiguationData":[OSD([sQuery(id+"F0.wireOp",EDGE,"E0"),sQuery(id+"F0.wireOp",EDGE,"E1")])]});
            hole(context, id + "F48", {"style" : HoleStyle.SIMPLE, "endStyle" : HoleEndStyle.BLIND, "standardTappedOrClearance" : lookupTablePath({ "standard" : "ISO", "engagement" : "75%", "pitch" : "0.75 mm", "size" : "M4", "type" : "Tapped" }), "standardBlindInLast" : lookupTablePath({ "standard" : "ISO", "engagement" : "75%", "pitch" : "0.75 mm", "size" : "M4", "type" : "Tapped" }), "holeDiameter" : 3.2 * mm, "holeDepth" : 20 * mm, "startFromSketch" : true, "locations" : qUnion([Q0]), "scope" : qUnion([Q1])});
        }
        {
            var Q0;
            Q0=makeQuery(id+"F3.boolean.opBoolean","COPY",FACE,{"derivedFrom":makeQuery(id+"F3.opExtrude","SWEPT_FACE",FACE,{"disambiguationData":[OSD([sQuery(id+"F2.wireOp",EDGE,"E8")])]})});
            var sketch = newSketch(context, id + "F49", { "sketchPlane" : qUnion([Q0])});
            skCircle(sketch, "E74", {"center": v(0, -12.5) * mm, "radius": 1.75 * mm});
            skPoint(sketch, "E74.centerSnap0", {"position": v(-10.1, -12.5) * mm});
            skPoint(sketch, "E74.centerSnap1", {"position": v(0, 0) * mm});
            skSolve(sketch);
        }
        {
            var Q0;
            Q0=sQuery(id+"F49.wireOp",VERTEX,"E74.center");
            var Q1;
            Q1=makeQuery(id+"F1.opExtrude","SWEPT_BODY",BODY,{"disambiguationData":[OSD([sQuery(id+"F0.wireOp",EDGE,"E0"),sQuery(id+"F0.wireOp",EDGE,"E1")])]});
            hole(context, id + "F50", {"style" : HoleStyle.SIMPLE, "endStyle" : HoleEndStyle.BLIND, "standardTappedOrClearance" : lookupTablePath({ "standard" : "ISO", "engagement" : "75%", "pitch" : "0.75 mm", "size" : "M4", "type" : "Tapped" }), "standardBlindInLast" : lookupTablePath({ "standard" : "ISO", "engagement" : "75%", "pitch" : "0.75 mm", "size" : "M4", "type" : "Tapped" }), "holeDiameter" : 3.2 * mm, "holeDepth" : 20 * mm, "startFromSketch" : true, "locations" : qUnion([Q0]), "scope" : qUnion([Q1])});
        }
        {
            var Q0;
            Q0=makeQuery(id+"F3.boolean.opBoolean","COPY",FACE,{"derivedFrom":makeQuery(id+"F3.opExtrude","SWEPT_FACE",FACE,{"disambiguationData":[OSD([sQuery(id+"F2.wireOp",EDGE,"E10")])]})});
            var sketch = newSketch(context, id + "F51", { "sketchPlane" : qUnion([Q0])});
            skCircle(sketch, "E75", {"center": v(-12.5, 0) * mm, "radius": 1.75 * mm});
            skPoint(sketch, "E75.centerSnap0", {"position": v(-12.5, 10.1) * mm});
            skPoint(sketch, "E75.centerSnap1", {"position": v(0, 0) * mm});
            skSolve(sketch);
        }
        {
            var Q0;
            Q0=sQuery(id+"F51.wireOp",VERTEX,"E75.center");
            var Q1;
            Q1=makeQuery(id+"F1.opExtrude","SWEPT_BODY",BODY,{"disambiguationData":[OSD([sQuery(id+"F0.wireOp",EDGE,"E0"),sQuery(id+"F0.wireOp",EDGE,"E1")])]});
            hole(context, id + "F52", {"style" : HoleStyle.SIMPLE, "endStyle" : HoleEndStyle.BLIND, "standardTappedOrClearance" : lookupTablePath({ "standard" : "ISO", "engagement" : "75%", "pitch" : "0.75 mm", "size" : "M4", "type" : "Tapped" }), "standardBlindInLast" : lookupTablePath({ "standard" : "ISO", "engagement" : "75%", "pitch" : "0.75 mm", "size" : "M4", "type" : "Tapped" }), "holeDiameter" : 3.2 * mm, "holeDepth" : 20 * mm, "startFromSketch" : true, "locations" : qUnion([Q0]), "scope" : qUnion([Q1])});
        }
        {
            var Q0;
            Q0=makeQuery(id+"F3.boolean.opBoolean","COPY",FACE,{"derivedFrom":makeQuery(id+"F3.opExtrude","SWEPT_FACE",FACE,{"disambiguationData":[OSD([sQuery(id+"F2.wireOp",EDGE,"E12")])]})});
            var sketch = newSketch(context, id + "F53", { "sketchPlane" : qUnion([Q0])});
            skCircle(sketch, "E76", {"center": v(-12.5, 0) * mm, "radius": 1.75 * mm});
            skPoint(sketch, "E76.centerSnap0", {"position": v(-12.5, 10.1) * mm});
            skSolve(sketch);
        }
        {
            var Q0;
            Q0=sQuery(id+"F53.wireOp",VERTEX,"E76.center");
            var Q1;
            Q1=makeQuery(id+"F1.opExtrude","SWEPT_BODY",BODY,{"disambiguationData":[OSD([sQuery(id+"F0.wireOp",EDGE,"E0"),sQuery(id+"F0.wireOp",EDGE,"E1")])]});
            hole(context, id + "F54", {"style" : HoleStyle.SIMPLE, "endStyle" : HoleEndStyle.BLIND, "standardTappedOrClearance" : lookupTablePath({ "standard" : "ISO", "engagement" : "75%", "pitch" : "0.75 mm", "size" : "M4", "type" : "Tapped" }), "standardBlindInLast" : lookupTablePath({ "standard" : "ISO", "engagement" : "75%", "pitch" : "0.75 mm", "size" : "M4", "type" : "Tapped" }), "holeDiameter" : 3.2 * mm, "holeDepth" : 20 * mm, "startFromSketch" : true, "locations" : qUnion([Q0]), "scope" : qUnion([Q1])});
        }
        {
            var Q0;
            Q0=qCreatedBy(makeId("Right.planeOp"),FACE);
            var sketch = newSketch(context, id + "F55", { "sketchPlane" : qUnion([Q0])});
            skCircle(sketch, "E77", {"center": v(-12.5, -0.36) * mm, "radius": 2.5 * mm});
            skSolve(sketch);
        }
        {
            var Q0;
            Q0=sQuery(id+"F55.wireOp",VERTEX,"E77.center");
            var Q1;
            Q1=makeQuery(id+"F1.opExtrude","SWEPT_BODY",BODY,{"disambiguationData":[OSD([sQuery(id+"F0.wireOp",EDGE,"E0"),sQuery(id+"F0.wireOp",EDGE,"E1")])]});
            hole(context, id + "F56", {"style" : HoleStyle.SIMPLE, "endStyle" : HoleEndStyle.BLIND, "standardTappedOrClearance" : lookupTablePath({ "standard" : "ISO", "engagement" : "75%", "pitch" : "1 mm", "size" : "M6", "type" : "Tapped" }), "standardBlindInLast" : lookupTablePath({ "standard" : "ISO", "engagement" : "75%", "pitch" : "1 mm", "size" : "M6", "type" : "Tapped" }), "holeDiameter" : 5 * mm, "holeDepth" : 100 * mm, "startFromSketch" : true, "locations" : qUnion([Q0]), "scope" : qUnion([Q1]), "majorDiameter" : 6 * mm});
        }
        {
            var Q0;
            Q0=qCreatedBy(makeId("Right.planeOp"),FACE);
            var sketch = newSketch(context, id + "F57", { "sketchPlane" : qUnion([Q0])});
            skCircle(sketch, "E78", {"center": v(-12.55, 0) * mm, "radius": 2.5 * mm});
            skSolve(sketch);
        }
        {
            var Q0;
            Q0=sQuery(id+"F57.wireOp",VERTEX,"E78.center");
            var Q1;
            Q1=makeQuery(id+"F1.opExtrude","SWEPT_BODY",BODY,{"disambiguationData":[OSD([sQuery(id+"F0.wireOp",EDGE,"E0"),sQuery(id+"F0.wireOp",EDGE,"E1")])]});
            hole(context, id + "F58", {"style" : HoleStyle.SIMPLE, "endStyle" : HoleEndStyle.BLIND, "oppositeDirection" : true, "standardTappedOrClearance" : lookupTablePath({ "standard" : "ISO", "engagement" : "75%", "pitch" : "1 mm", "size" : "M6", "type" : "Tapped" }), "standardBlindInLast" : lookupTablePath({ "standard" : "ISO", "engagement" : "75%", "pitch" : "1 mm", "size" : "M6", "type" : "Tapped" }), "holeDiameter" : 5 * mm, "holeDepth" : 100 * mm, "startFromSketch" : true, "locations" : qUnion([Q0]), "scope" : qUnion([Q1]), "majorDiameter" : 6 * mm});
        }
    });
